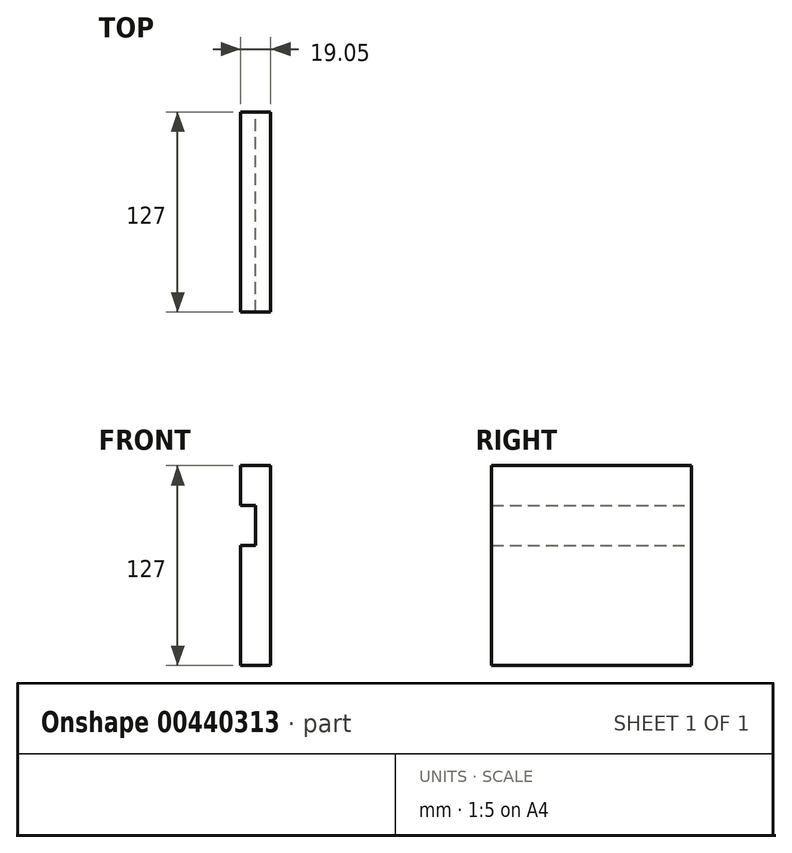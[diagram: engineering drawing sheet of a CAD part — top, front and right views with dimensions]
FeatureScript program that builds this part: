
annotation { "Feature Type Name" : "Feature", "Feature Type Description" : "" }
export const myFeature = defineFeature(function(context is Context, id is Id, definition is map)
    precondition{}
    {
        {
            var Q0;
            Q0=qCreatedBy(makeId("Front.planeOp"),FACE);
            var sketch = newSketch(context, id + "F0", { "sketchPlane" : qUnion([Q0])});
            skLineSegment(sketch, "E0", {"start": v(0, 0) * mm, "end": v(-19.05, 0) * mm});
            skLineSegment(sketch, "E1", {"start": v(0, 0) * mm, "end": v(0, 127) * mm});
            skLineSegment(sketch, "E2", {"start": v(0, 127) * mm, "end": v(-19.05, 127) * mm});
            skLineSegment(sketch, "E3", {"start": v(-19.05, 127) * mm, "end": v(-19.05, 101.6) * mm});
            skLineSegment(sketch, "E4", {"start": v(-19.05, 101.6) * mm, "end": v(-9.52, 101.6) * mm});
            skLineSegment(sketch, "E5", {"start": v(-9.52, 101.6) * mm, "end": v(-9.52, 76.2) * mm});
            skLineSegment(sketch, "E6", {"start": v(-9.52, 76.2) * mm, "end": v(-19.05, 76.2) * mm});
            skLineSegment(sketch, "E7", {"start": v(-19.05, 76.2) * mm, "end": v(-19.05, 0) * mm});
            skSolve(sketch);
        }
        {
            var Q0;
            Q0 = qSketchRegion(id + "F0", true);
            extrude(context, id + "F1", {"entities" : qUnion([Q0]), "depth" : 127 * mm});
        }
    });
